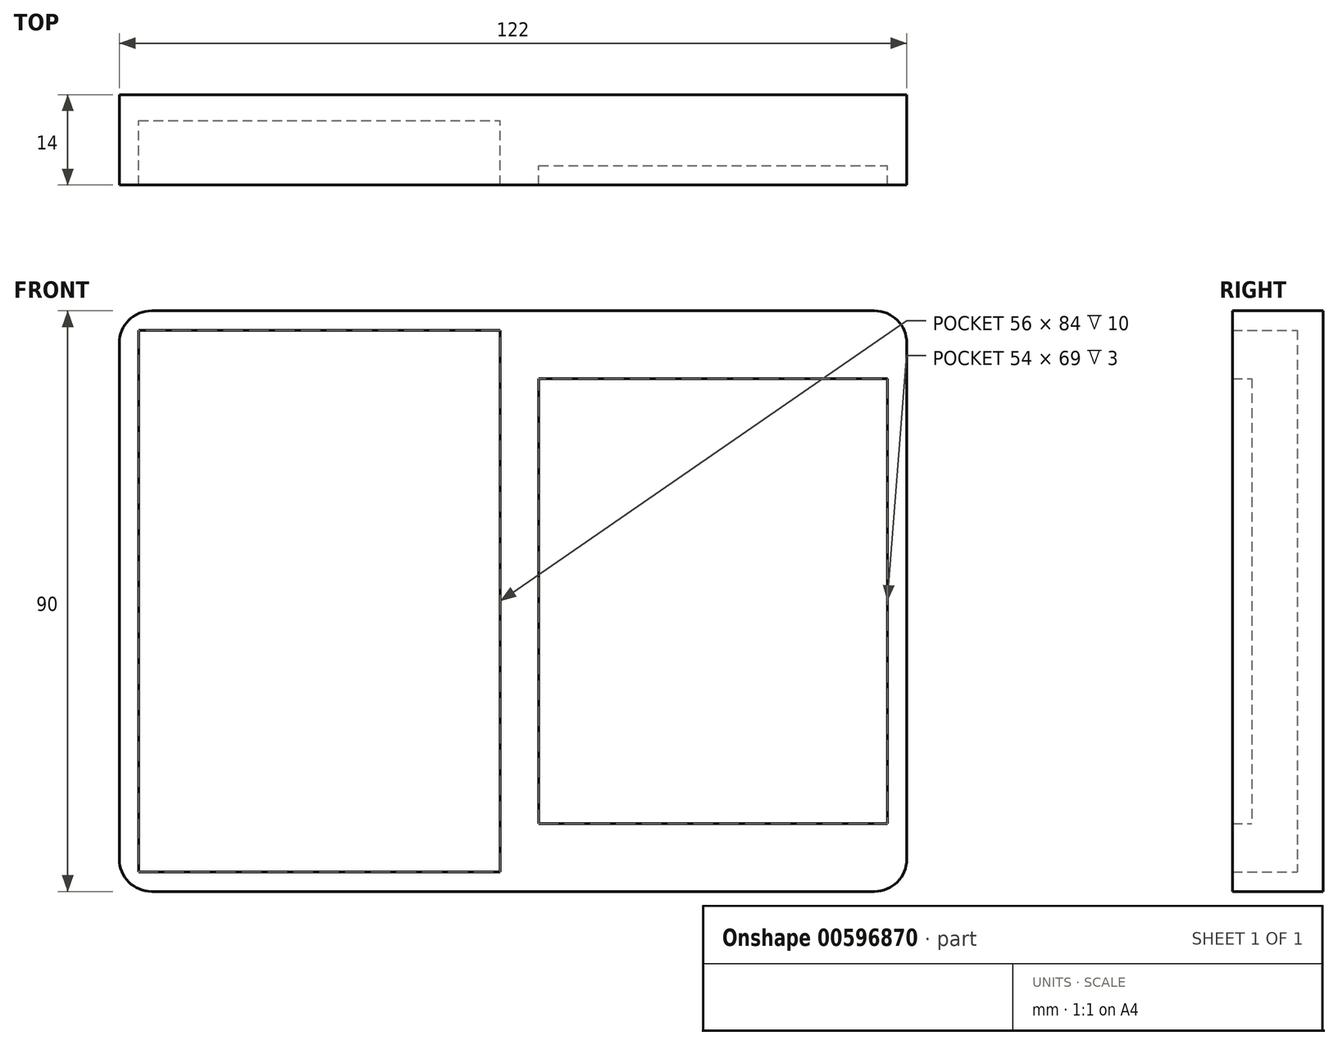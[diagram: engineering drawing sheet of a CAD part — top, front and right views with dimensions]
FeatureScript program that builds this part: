
annotation { "Feature Type Name" : "Feature", "Feature Type Description" : "" }
export const myFeature = defineFeature(function(context is Context, id is Id, definition is map)
    precondition{}
    {
        {
            var Q0;
            Q0=qCreatedBy(makeId("Front.planeOp"),FACE);
            var sketch = newSketch(context, id + "F0", { "sketchPlane" : qUnion([Q0])});
            skLineSegment(sketch, "E0.bottom", {"start": v(-74.47, 41.92) * mm, "end": v(-18.47, 41.92) * mm});
            skLineSegment(sketch, "E0.top", {"start": v(-74.47, -42.08) * mm, "end": v(-18.47, -42.08) * mm});
            skLineSegment(sketch, "E0.left", {"start": v(-74.47, 41.92) * mm, "end": v(-74.47, -42.08) * mm});
            skLineSegment(sketch, "E0.right", {"start": v(-18.47, 41.92) * mm, "end": v(-18.47, -42.08) * mm});
            skLineSegment(sketch, "E1.bottom", {"start": v(-12.47, 34.42) * mm, "end": v(41.53, 34.42) * mm});
            skLineSegment(sketch, "E1.top", {"start": v(-12.47, -34.58) * mm, "end": v(41.53, -34.58) * mm});
            skLineSegment(sketch, "E1.left", {"start": v(-12.47, 34.42) * mm, "end": v(-12.47, -34.58) * mm});
            skLineSegment(sketch, "E1.right", {"start": v(41.53, 34.42) * mm, "end": v(41.53, -34.58) * mm});
            skLineSegment(sketch, "E2.bottom", {"start": v(-77.47, 44.92) * mm, "end": v(44.53, 44.92) * mm});
            skLineSegment(sketch, "E2.top", {"start": v(-77.47, -45.08) * mm, "end": v(44.53, -45.08) * mm});
            skLineSegment(sketch, "E2.left", {"start": v(-77.47, 44.92) * mm, "end": v(-77.47, -45.08) * mm});
            skLineSegment(sketch, "E2.right", {"start": v(44.53, 44.92) * mm, "end": v(44.53, -45.08) * mm});
            skSolve(sketch);
        }
        {
            var Q0;
            Q0=makeQuery(id+"F0.imprint","IMPRINT",FACE,{"disambiguationData":[TD([[makeQuery(id+"F0.imprint","IMPRINT",EDGE,{"derivedFrom":sQuery(id+"F0.wireOp",EDGE,"E0.bottom")}),1.0]])]});
            extrude(context, id + "F1", {"entities" : qUnion([Q0]), "depth" : 14 * mm, "offsetDistance" : 25 * mm});
        }
        {
            var Q0;
            Q0=makeQuery(id+"F0.imprint","IMPRINT",FACE,{"disambiguationData":[TD([[makeQuery(id+"F0.imprint","IMPRINT",EDGE,{"derivedFrom":sQuery(id+"F0.wireOp",EDGE,"E0.bottom")}),-1.0]])]});
            extrude(context, id + "F2", {"entities" : qUnion([Q0]), "operationType" : NewBodyOperationType.ADD, "depth" : 4 * mm, "offsetDistance" : 25 * mm});
        }
        {
            var Q0;
            Q0=makeQuery(id+"F0.imprint","IMPRINT",FACE,{"disambiguationData":[TD([[makeQuery(id+"F0.imprint","IMPRINT",EDGE,{"derivedFrom":sQuery(id+"F0.wireOp",EDGE,"E1.bottom")}),-1.0]])]});
            extrude(context, id + "F3", {"entities" : qUnion([Q0]), "operationType" : NewBodyOperationType.ADD, "depth" : 11 * mm, "offsetDistance" : 25 * mm});
        }
        {
            var Q0;
            Q0=makeQuery(id+"F1.opExtrude","SWEPT_EDGE",EDGE,{"disambiguationData":[OSD([sQuery(id+"F0.wireOp",EDGE,"E2.top"),sQuery(id+"F0.wireOp",EDGE,"E2.left")])]});
            var Q1;
            Q1=makeQuery(id+"F1.opExtrude","SWEPT_EDGE",EDGE,{"disambiguationData":[OSD([sQuery(id+"F0.wireOp",EDGE,"E2.top"),sQuery(id+"F0.wireOp",EDGE,"E2.right")])]});
            var Q2;
            Q2=makeQuery(id+"F1.opExtrude","SWEPT_EDGE",EDGE,{"disambiguationData":[OSD([sQuery(id+"F0.wireOp",EDGE,"E2.bottom"),sQuery(id+"F0.wireOp",EDGE,"E2.right")])]});
            var Q3;
            Q3=makeQuery(id+"F1.opExtrude","SWEPT_EDGE",EDGE,{"disambiguationData":[OSD([sQuery(id+"F0.wireOp",EDGE,"E2.bottom"),sQuery(id+"F0.wireOp",EDGE,"E2.left")])]});
            fillet(context, id + "F4", {"entities" : qUnion([Q0, Q1, Q2, Q3]), "radius" : 5 * mm, "tangentPropagation" : true, "allowEdgeOverflow" : false});
        }
    });
